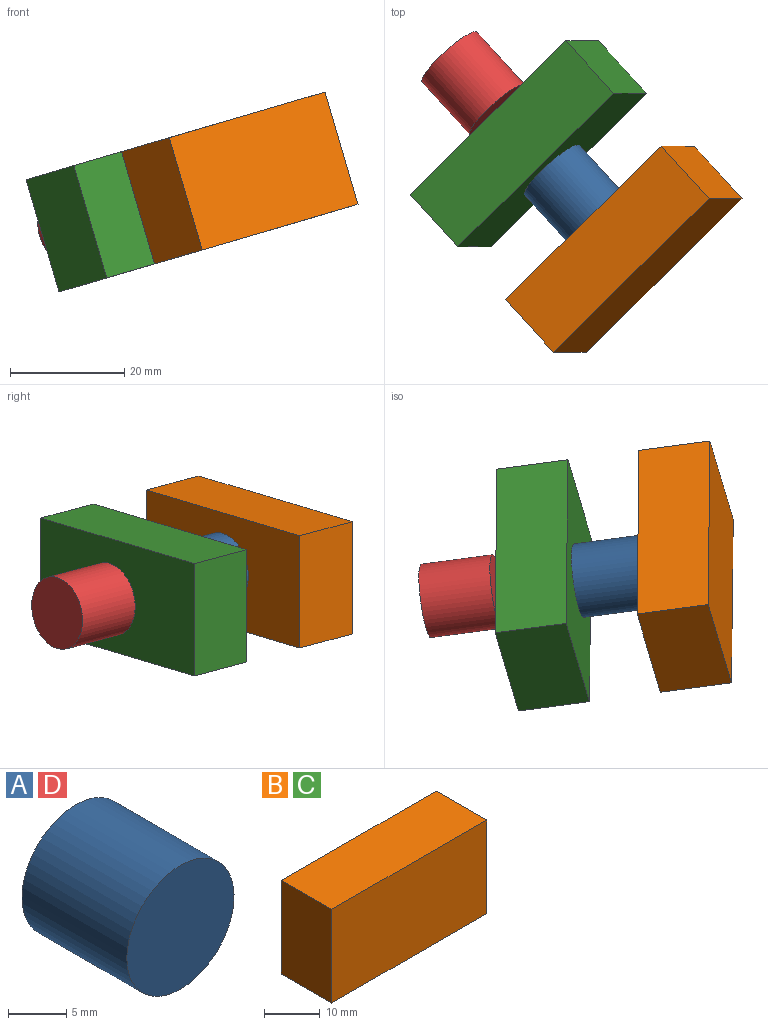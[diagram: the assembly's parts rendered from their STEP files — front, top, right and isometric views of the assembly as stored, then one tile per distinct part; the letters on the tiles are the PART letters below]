
ASSEMBLY  parts=4 mates=3
PART A: 3 faces, bbox 13x12.7x13 mm
  f0: cylinder r=6.49mm len=12.98mm, axis (0,1,0), area 517.8mm2, adj f1,f2
  f1: plane 12.98x12.98mm, normal (0,-1,0), area 132.3mm2, adj f0
  f2: plane 12.98x12.98mm, normal (0,1,0), area 132.3mm2, adj f0
PART B: 6 faces, bbox 39.2x12.7x20.5 mm
  f0: plane 20.51x12.7mm, normal (-1,0,0), area 260.4mm2, adj f1,f3,f4,f5
  f1: plane 39.15x12.7mm, normal (0,0,-1), area 497.2mm2, adj f0,f2,f4,f5
  f2: plane 20.51x12.7mm, normal (1,0,0), area 260.4mm2, adj f1,f3,f4,f5
  f3: plane 39.15x12.7mm, normal (0,0,1), area 497.2mm2, adj f0,f2,f4,f5
  f4: plane 39.15x20.51mm, normal (0,-1,0), area 802.9mm2, adj f0,f1,f2,f3
  f5: plane 39.15x20.51mm, normal (0,1,0), area 802.9mm2, adj f0,f1,f2,f3
PART C: same geometry as B
PART D: same geometry as A
PLACE A rot(axis=(0.14,-0.06,-0.99),137.1deg) t=(164.8,166.8,60.61)mm
PLACE B rot(axis=(0.14,-0.06,-0.99),137.1deg) t=(149.4,134.15,55.96)mm
PLACE C rot(axis=(-0.37,0.93,-0.05),164.8deg) t=(89.17,161.85,168.48)mm
PLACE D rot(axis=(0.14,-0.06,-0.99),137.1deg) t=(146.83,186.62,55.34)mm
MATE slider D.f0 <-> C.f5  axis (0.66,-0.73,0.19) through (140.41,197.55,118.41)mm
MATE fastened A.f0 <-> C.f4  axis (-0.66,0.73,-0.19) through (150.01,186.96,121.22)mm
MATE fastened B.f4 <-> A.f0  axis (-0.66,0.73,-0.19) through (158.38,177.72,123.68)mm
